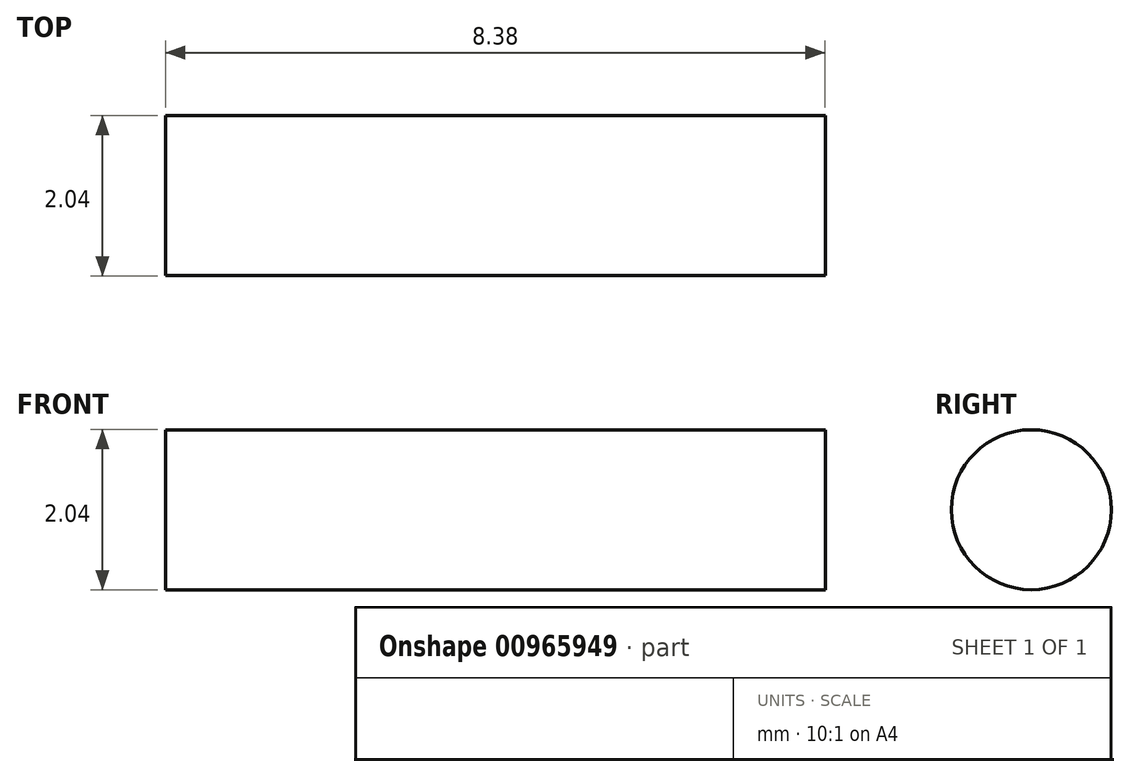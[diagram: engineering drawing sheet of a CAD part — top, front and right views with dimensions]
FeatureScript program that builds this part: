
annotation { "Feature Type Name" : "Feature", "Feature Type Description" : "" }
export const myFeature = defineFeature(function(context is Context, id is Id, definition is map)
    precondition{}
    {
        {
            var Q0;
            Q0=qCreatedBy(makeId("Right.planeOp"),FACE);
            var sketch = newSketch(context, id + "F0", { "sketchPlane" : qUnion([Q0])});
            skCircle(sketch, "E0", {"center": v(0, 0) * mm, "radius": 1.02 * mm});
            skSolve(sketch);
        }
        {
            var Q0;
            Q0=makeQuery(id+"F0.imprint","IMPRINT",FACE,{"disambiguationData":[TD([[makeQuery(id+"F0.imprint","IMPRINT",EDGE,{"derivedFrom":sQuery(id+"F0.wireOp",EDGE,"E0")}),1.0]])]});
            extrude(context, id + "F1", {"entities" : qUnion([Q0]), "depth" : 8.38 * mm, "offsetDistance" : 25.4 * mm});
        }
    });
